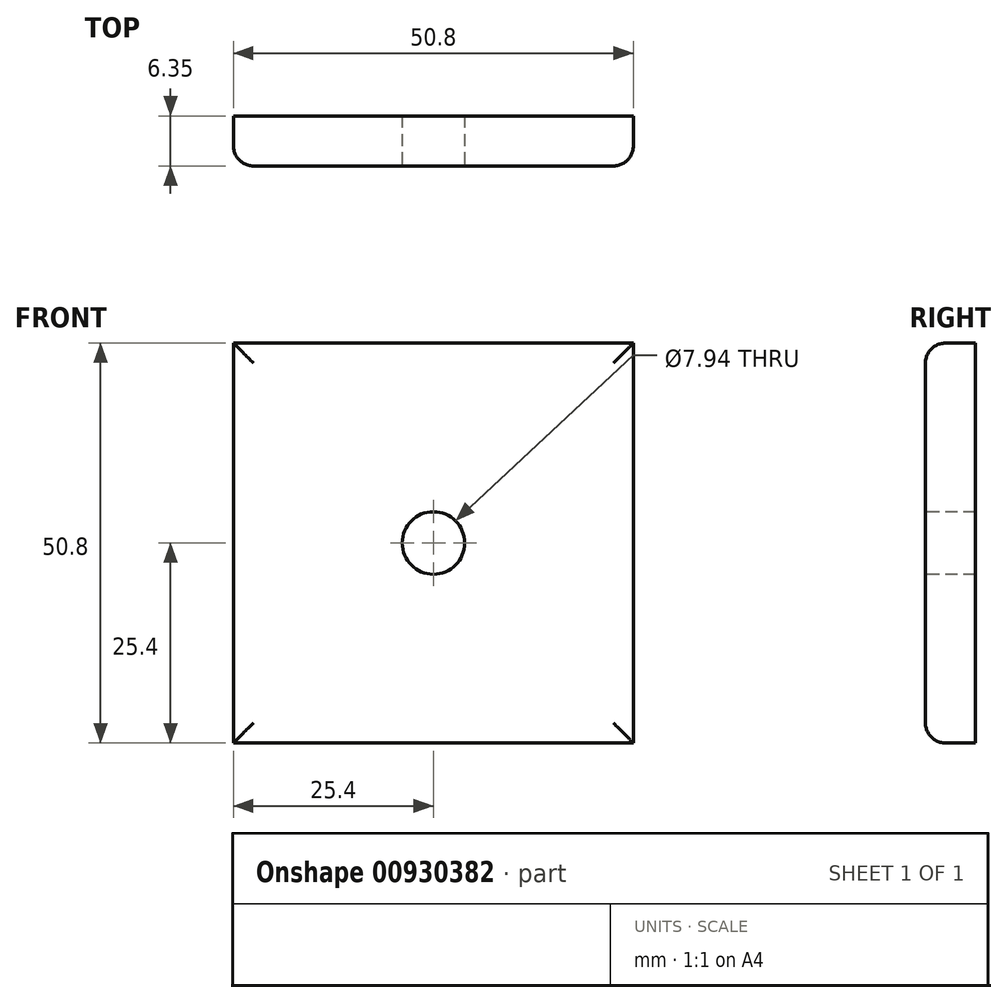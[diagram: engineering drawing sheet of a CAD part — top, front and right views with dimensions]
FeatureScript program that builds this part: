
annotation { "Feature Type Name" : "Feature", "Feature Type Description" : "" }
export const myFeature = defineFeature(function(context is Context, id is Id, definition is map)
    precondition{}
    {
        {
            var Q0;
            Q0=qCreatedBy(makeId("Front.planeOp"),FACE);
            var sketch = newSketch(context, id + "F0", { "sketchPlane" : qUnion([Q0])});
            skLineSegment(sketch, "E0.bottom", {"start": v(25.4, -25.4) * mm, "end": v(-25.4, -25.4) * mm});
            skLineSegment(sketch, "E0.top", {"start": v(25.4, 25.4) * mm, "end": v(-25.4, 25.4) * mm});
            skLineSegment(sketch, "E0.left", {"start": v(25.4, -25.4) * mm, "end": v(25.4, 25.4) * mm});
            skLineSegment(sketch, "E0.right", {"start": v(-25.4, -25.4) * mm, "end": v(-25.4, 25.4) * mm});
            skPoint(sketch, "E0.middle", {"position": v(0, 0) * mm});
            skSolve(sketch);
        }
        {
            var Q0;
            Q0 = qSketchRegion(id + "F0", true);
            extrude(context, id + "F1", {"entities" : qUnion([Q0]), "depth" : 6.35 * mm, "offsetDistance" : 25.4 * mm});
        }
        {
            var Q0;
            Q0=makeQuery(id+"F1.opExtrude","CAP_EDGE",EDGE,{"disambiguationData":[OSD([sQuery(id+"F0.wireOp",EDGE,"E0.left")])],"isStart":false});
            var Q1;
            Q1=makeQuery(id+"F1.opExtrude","CAP_EDGE",EDGE,{"disambiguationData":[OSD([sQuery(id+"F0.wireOp",EDGE,"E0.bottom")])],"isStart":false});
            var Q2;
            Q2=makeQuery(id+"F1.opExtrude","CAP_EDGE",EDGE,{"disambiguationData":[OSD([sQuery(id+"F0.wireOp",EDGE,"E0.right")])],"isStart":false});
            var Q3;
            Q3=makeQuery(id+"F1.opExtrude","CAP_EDGE",EDGE,{"disambiguationData":[OSD([sQuery(id+"F0.wireOp",EDGE,"E0.top")])],"isStart":false});
            fillet(context, id + "F2", {"entities" : qUnion([Q0, Q1, Q2, Q3]), "radius" : 2.54 * mm, "tangentPropagation" : true, "allowEdgeOverflow" : false});
        }
        {
            var Q0;
            Q0=makeQuery(id+"F1.opExtrude","CAP_FACE",FACE,{"disambiguationData":[OSD([sQuery(id+"F0.wireOp",EDGE,"E0.bottom"),sQuery(id+"F0.wireOp",EDGE,"E0.top"),sQuery(id+"F0.wireOp",EDGE,"E0.left"),sQuery(id+"F0.wireOp",EDGE,"E0.right")])],"isStart":false});
            var sketch = newSketch(context, id + "F3", { "sketchPlane" : qUnion([Q0])});
            skPoint(sketch, "E1", {"position": v(0, 0) * mm});
            skSolve(sketch);
        }
        {
            var Q0;
            Q0=sQuery(id+"F3.wireOp",VERTEX,"E1");
            var Q1;
            Q1=makeQuery(id+"F1.opExtrude","SWEPT_BODY",BODY,{"disambiguationData":[OSD([sQuery(id+"F0.wireOp",EDGE,"E0.bottom"),sQuery(id+"F0.wireOp",EDGE,"E0.top"),sQuery(id+"F0.wireOp",EDGE,"E0.left"),sQuery(id+"F0.wireOp",EDGE,"E0.right")])]});
            hole(context, id + "F4", {"style" : HoleStyle.SIMPLE, "endStyle" : HoleEndStyle.THROUGH, "standardTappedOrClearance" : lookupTablePath({ "standard" : "ANSI", "engagement" : "75%", "pitch" : "16 tpi", "size" : "3/8", "type" : "Tapped" }), "standardBlindInLast" : lookupTablePath({ "standard" : "ANSI", "fit" : "Normal", "engagement" : "75%", "pitch" : "16 tpi", "size" : "3/8", "type" : "Clearance & tapped" }), "holeDiameter" : 7.94 * mm, "majorDiameter" : 9.52 * mm, "showTappedDepth" : true, "isTappedThrough" : true, "tappedDepth" : 12.7 * mm, "tapClearance" : 3, "locations" : qUnion([Q0]), "scope" : qUnion([Q1])});
        }
    });
